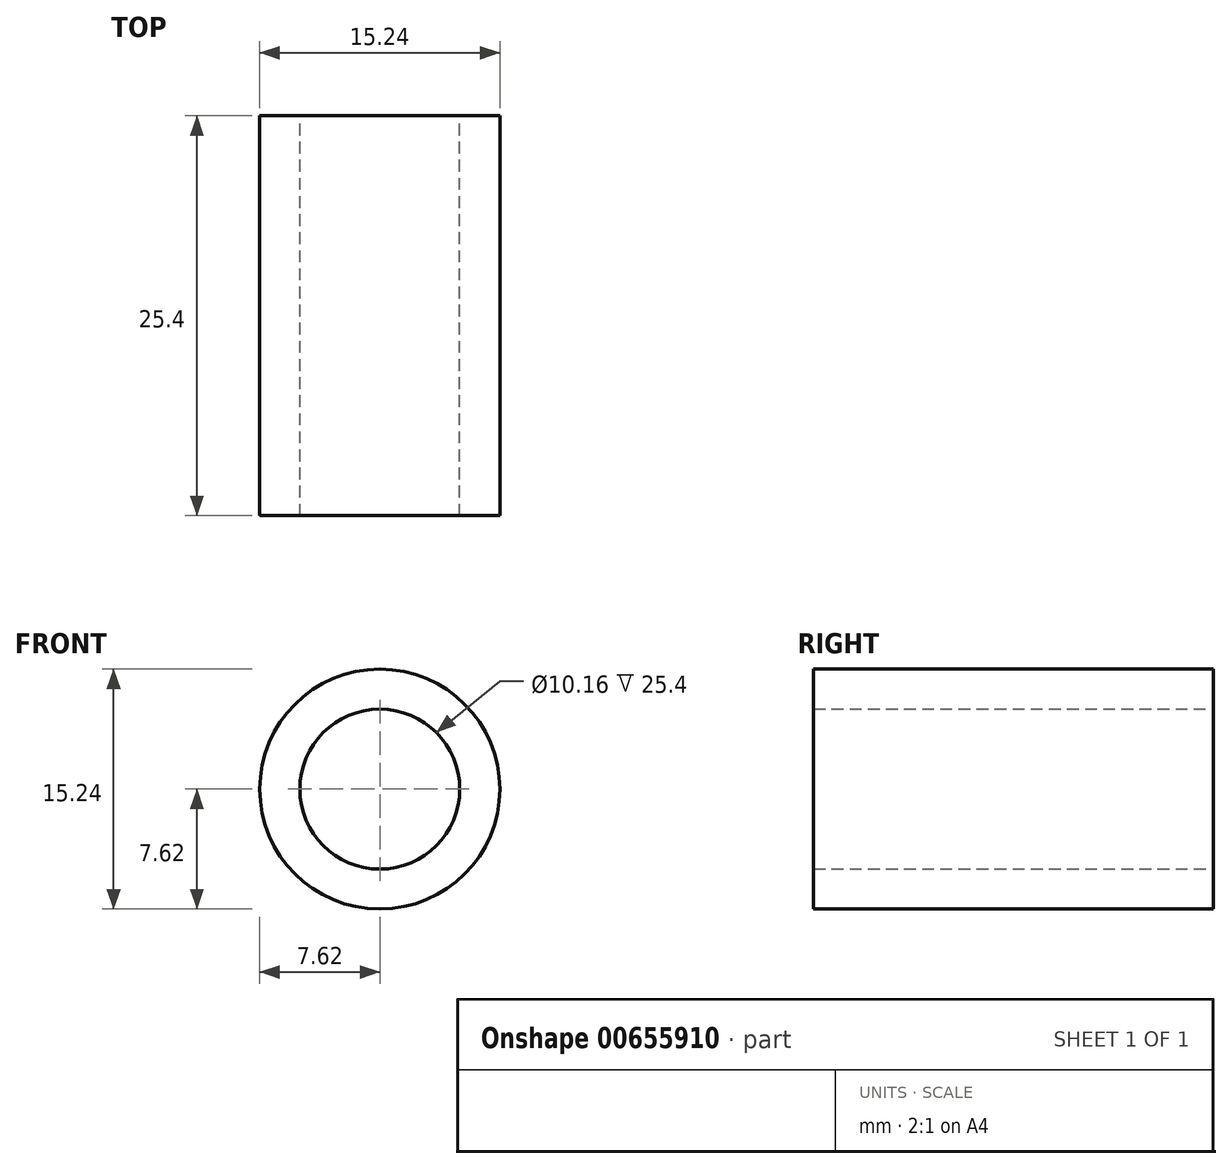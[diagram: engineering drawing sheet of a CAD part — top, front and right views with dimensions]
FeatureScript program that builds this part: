
annotation { "Feature Type Name" : "Feature", "Feature Type Description" : "" }
export const myFeature = defineFeature(function(context is Context, id is Id, definition is map)
    precondition{}
    {
        {
            var Q0;
            Q0=qCreatedBy(makeId("Front.planeOp"),FACE);
            var sketch = newSketch(context, id + "F0", { "sketchPlane" : qUnion([Q0])});
            skCircle(sketch, "E0", {"center": v(0, 0) * mm, "radius": 7.62 * mm});
            skCircle(sketch, "E1", {"center": v(0, 0) * mm, "radius": 5.08 * mm});
            skSolve(sketch);
        }
        {
            var Q0;
            Q0=makeQuery(id+"F0.imprint","IMPRINT",FACE,{"disambiguationData":[TD([[makeQuery(id+"F0.imprint","IMPRINT",EDGE,{"derivedFrom":sQuery(id+"F0.wireOp",EDGE,"E0")}),1.0]])]});
            extrude(context, id + "F1", {"entities" : qUnion([Q0]), "depth" : 25.4 * mm, "offsetDistance" : 25.4 * mm});
        }
    });
